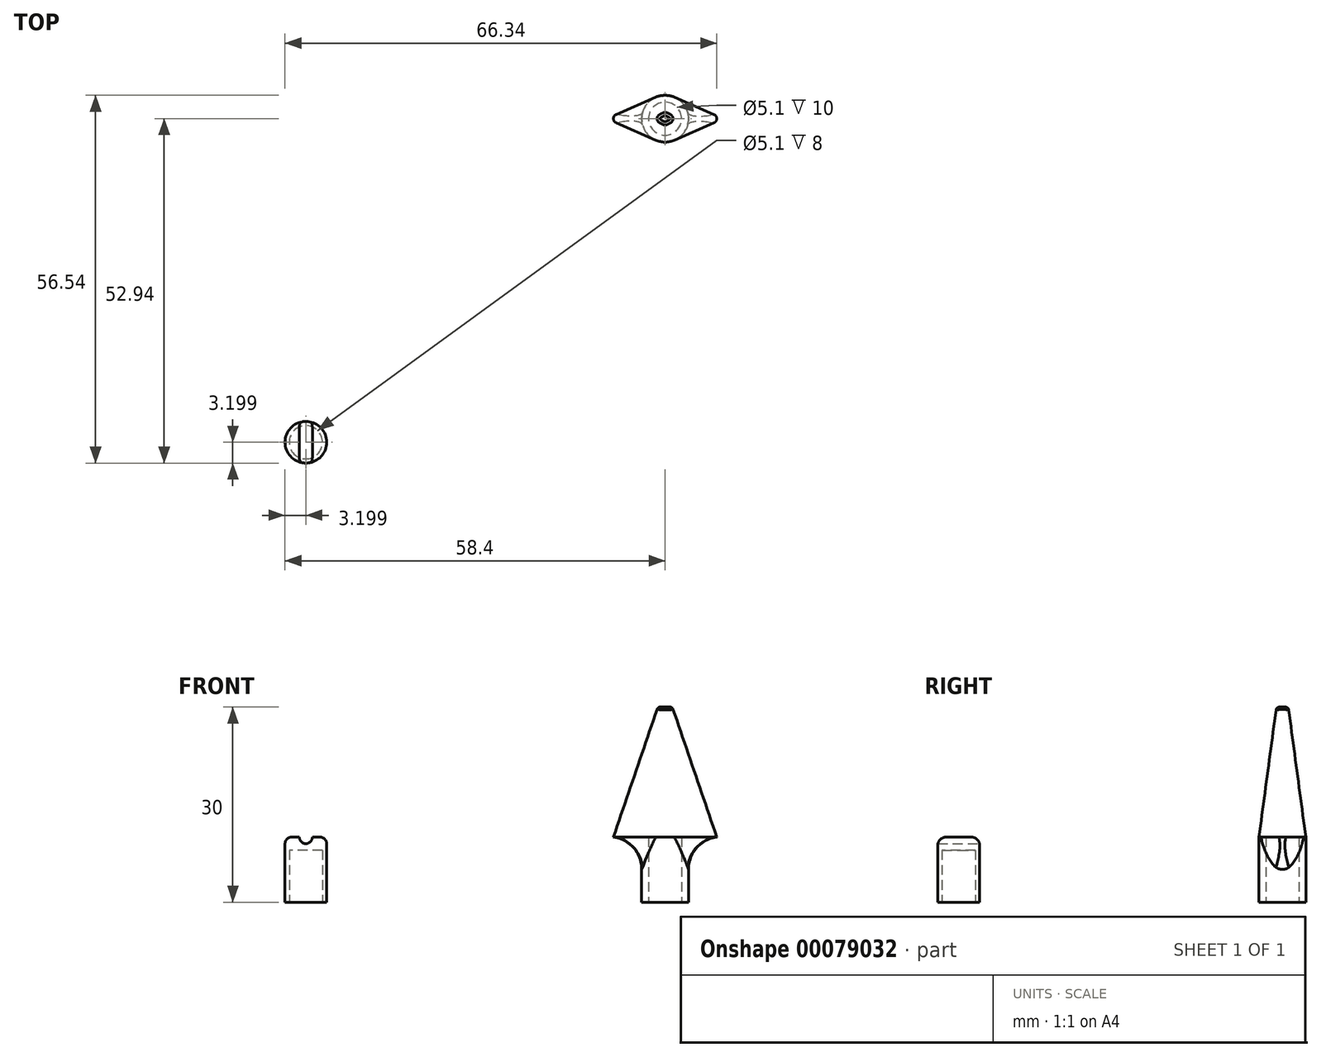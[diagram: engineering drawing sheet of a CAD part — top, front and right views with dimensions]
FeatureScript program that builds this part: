
annotation { "Feature Type Name" : "Feature", "Feature Type Description" : "" }
export const myFeature = defineFeature(function(context is Context, id is Id, definition is map)
    precondition{}
    {
        {
            var Q0;
            Q0=qCreatedBy(makeId("Top.planeOp"),FACE);
            var sketch = newSketch(context, id + "F0", { "sketchPlane" : qUnion([Q0])});
            skCircle(sketch, "E0", {"center": v(0, 0) * mm, "radius": 2.55 * mm});
            skCircle(sketch, "E1", {"center": v(0, 0) * mm, "radius": 3.6 * mm});
            skSolve(sketch);
        }
        {
            var Q0;
            Q0=makeQuery(id+"F0.imprint","IMPRINT",FACE,{"disambiguationData":[TD([[makeQuery(id+"F0.imprint","IMPRINT",EDGE,{"derivedFrom":sQuery(id+"F0.wireOp",EDGE,"E0")}),-1.0]])]});
            extrude(context, id + "F1", {"entities" : qUnion([Q0]), "depth" : 10 * mm});
        }
        {
            var Q0;
            Q0=makeQuery(id+"F1.opExtrude","CAP_FACE",FACE,{"disambiguationData":[OSD([sQuery(id+"F0.wireOp",EDGE,"E0"),sQuery(id+"F0.wireOp",EDGE,"E1")])],"isStart":false});
            var sketch = newSketch(context, id + "F2", { "sketchPlane" : qUnion([Q0])});
            skLineSegment(sketch, "E2", {"start": v(0, 0) * mm, "end": v(0, 3.6) * mm, "construction": true});
            skLineSegment(sketch, "E3", {"start": v(0, 0) * mm, "end": v(0, -3.6) * mm, "construction": true});
            skLineSegment(sketch, "E4", {"start": v(7.51, 0.65) * mm, "end": v(1.44, 3.3) * mm});
            skLineSegment(sketch, "E5.MirrorCS", {"start": v(-7.51, 0.65) * mm, "end": v(-1.44, 3.3) * mm});
            skLineSegment(sketch, "E6.MirrorCS", {"start": v(7.51, -0.65) * mm, "end": v(1.44, -3.3) * mm});
            skLineSegment(sketch, "E7.MirrorCS", {"start": v(-7.51, -0.65) * mm, "end": v(-1.44, -3.3) * mm});
            skPoint(sketch, "E8.visualSharp", {"position": v(9, 0) * mm});
            skArc(sketch, "E8.filletArc", {"start": v(7.51, -0.65) * mm, "mid": v(7.94, 0) * mm, "end": v(7.51, 0.65) * mm});
            skPoint(sketch, "E9.visualSharp", {"position": v(-9, 0) * mm});
            skArc(sketch, "E9.filletArc", {"start": v(-7.51, 0.65) * mm, "mid": v(-7.94, 0) * mm, "end": v(-7.51, -0.65) * mm});
            skArc(sketch, "E10", {"start": v(-1.44, 3.3) * mm, "mid": v(0, 3.6) * mm, "end": v(1.44, 3.3) * mm});
            skArc(sketch, "E11", {"start": v(-1.44, -3.3) * mm, "mid": v(0, -3.6) * mm, "end": v(1.44, -3.3) * mm});
            skSolve(sketch);
        }
        {
            var Q0;
            {var subQ0=sQuery(id+"F2.wireOp",EDGE,"E4");Q0=makeQuery(id+"F2.imprint","IMPRINT",FACE,{"disambiguationData":[TD([[makeQuery(id+"F2.imprint","IMPRINT",EDGE,{"derivedFrom":subQ0}),1.0]])]});}
            cPlane(context, id + "F3", {"entities" : qUnion([Q0]), "cplaneType" : CPlaneType.OFFSET, "offset" : 20 * mm, "width" : 150 * mm, "height" : 150 * mm});
        }
        {
            var Q0;
            Q0=qCreatedBy(id+"F3.planeOp",FACE);
            var sketch = newSketch(context, id + "F4", { "sketchPlane" : qUnion([Q0])});
            skLineSegment(sketch, "E12", {"start": v(0, 0) * mm, "end": v(0, 1) * mm, "construction": true});
            skLineSegment(sketch, "E13", {"start": v(0, 0) * mm, "end": v(0, -1) * mm, "construction": true});
            skLineSegment(sketch, "E14", {"start": v(0.32, 0.83) * mm, "end": v(0.72, 0.63) * mm});
            skLineSegment(sketch, "E15.MirrorCS", {"start": v(-0.32, 0.83) * mm, "end": v(-0.72, 0.63) * mm});
            skLineSegment(sketch, "E16.MirrorCS", {"start": v(0.32, -0.83) * mm, "end": v(0.72, -0.63) * mm});
            skLineSegment(sketch, "E17.MirrorCS", {"start": v(-0.32, -0.83) * mm, "end": v(-0.72, -0.63) * mm});
            skPoint(sketch, "E18.visualSharp", {"position": v(0, 1) * mm});
            skArc(sketch, "E18.filletArc", {"start": v(0.32, 0.83) * mm, "mid": v(0, 0.91) * mm, "end": v(-0.32, 0.83) * mm});
            skPoint(sketch, "E19.visualSharp", {"position": v(1.95, 0) * mm});
            skArc(sketch, "E19.filletArc", {"start": v(0.72, -0.63) * mm, "mid": v(1.1, 0) * mm, "end": v(0.72, 0.63) * mm});
            skPoint(sketch, "E20.visualSharp", {"position": v(0, -1) * mm});
            skArc(sketch, "E20.filletArc", {"start": v(-0.32, -0.83) * mm, "mid": v(0, -0.91) * mm, "end": v(0.32, -0.83) * mm});
            skPoint(sketch, "E21.visualSharp", {"position": v(-1.95, 0) * mm});
            skArc(sketch, "E21.filletArc", {"start": v(-0.72, 0.63) * mm, "mid": v(-1.1, 0) * mm, "end": v(-0.72, -0.63) * mm});
            skSolve(sketch);
        }
        {
            var Q1;
            Q1 = qSketchRegion(id + "F2", true);
            var Q2;
            Q2 = qSketchRegion(id + "F4", true);
            loft(context, id + "F5", {"operationType" : NewBodyOperationType.ADD, "sheetProfilesArray" : [{ "sheetProfileEntities" : qUnion([Q1]) }, { "sheetProfileEntities" : qUnion([Q2]) }]});
        }
        {
            var Q0;
            Q0=makeQuery(id+"F5.boolean.opBoolean","SPLIT",EDGE,{"disambiguationData":[OD(0.0)],"derivedFrom":makeQuery(id+"F1.opExtrude","CAP_EDGE",EDGE,{"disambiguationData":[OSD([sQuery(id+"F0.wireOp",EDGE,"E1")])],"isStart":false})});
            var Q1;
            Q1=makeQuery(id+"F5.boolean.opBoolean","SPLIT",EDGE,{"disambiguationData":[OD(1.0)],"derivedFrom":makeQuery(id+"F1.opExtrude","CAP_EDGE",EDGE,{"disambiguationData":[OSD([sQuery(id+"F0.wireOp",EDGE,"E1")])],"isStart":false})});
            fillet(context, id + "F6", {"entities" : qUnion([Q0, Q1]), "radius" : 5 * mm, "tangentPropagation" : true, "allowEdgeOverflow" : false});
        }
        {
            var Q0;
            Q0=makeQuery(id+"F5.opLoft","MID_CAP_EDGE",EDGE,{"disambiguationData":[OSD([sQuery(id+"F4.wireOp",EDGE,"E15.MirrorCS"),sQuery(id+"F4.wireOp",EDGE,"E17.MirrorCS"),sQuery(id+"F4.wireOp",EDGE,"E21.filletArc")])],"capPos":1.0});
            fillet(context, id + "F7", {"entities" : qUnion([Q0]), "radius" : 0.5 * mm, "tangentPropagation" : true, "allowEdgeOverflow" : false});
        }
        {
            var Q0;
            Q0=qCreatedBy(makeId("Top.planeOp"),FACE);
            var sketch = newSketch(context, id + "F8", { "sketchPlane" : qUnion([Q0])});
            skCircle(sketch, "E22", {"center": v(-55.2, -49.74) * mm, "radius": 2.55 * mm});
            skCircle(sketch, "E23", {"center": v(-55.2, -49.74) * mm, "radius": 3.2 * mm});
            skSolve(sketch);
        }
        {
            var Q0;
            Q0 = qSketchRegion(id + "F8", true);
            extrude(context, id + "F9", {"entities" : qUnion([Q0]), "depth" : 8 * mm});
        }
        {
            var Q0;
            Q0=makeQuery(id+"F9.opExtrude","CAP_FACE",FACE,{"disambiguationData":[OSD([sQuery(id+"F8.wireOp",EDGE,"E22"),sQuery(id+"F8.wireOp",EDGE,"E23")])],"isStart":false});
            var sketch = newSketch(context, id + "F10", { "sketchPlane" : qUnion([Q0])});
            skCircle(sketch, "E24", {"center": v(-55.2, -49.74) * mm, "radius": 3.2 * mm});
            skSolve(sketch);
        }
        {
            var Q0;
            Q0=makeQuery(id+"F10.imprint","IMPRINT",FACE,{"disambiguationData":[TD([[makeQuery(id+"F10.imprint","IMPRINT",EDGE,{"derivedFrom":sQuery(id+"F10.wireOp",EDGE,"E24")}),1.0]])]});
            var Q1;
            Q1=makeQuery(id+"F10.imprint","IMPRINT",FACE,{"disambiguationData":[TD([[makeQuery(id+"F10.imprint","IMPRINT",EDGE,{"derivedFrom":makeQuery(id+"F9.opExtrude","CAP_EDGE",EDGE,{"disambiguationData":[OSD([sQuery(id+"F8.wireOp",EDGE,"E22")])],"isStart":false})}),1.0]])]});
            extrude(context, id + "F11", {"entities" : qUnion([Q0, Q1]), "operationType" : NewBodyOperationType.ADD, "depth" : 2 * mm});
        }
        {
            var Q0;
            Q0=makeQuery(id+"F11.opExtrude","CAP_FACE",FACE,{"disambiguationData":[OSD([sQuery(id+"F10.wireOp",EDGE,"E24")])],"isStart":false});
            var sketch = newSketch(context, id + "F12", { "sketchPlane" : qUnion([Q0])});
            skLineSegment(sketch, "E25", {"start": v(-55.2, -49.74) * mm, "end": v(-55.2, -46.54) * mm, "construction": true});
            skSolve(sketch);
        }
        {
            var Q0;
            Q0=qCreatedBy(makeId("Front.planeOp"),FACE);
            var sketch = newSketch(context, id + "F13", { "sketchPlane" : qUnion([Q0])});
            skCircle(sketch, "E26", {"center": v(-55.2, 10) * mm, "radius": 1 * mm});
            skSolve(sketch);
        }
        {
            var Q0;
            Q0=makeQuery(id+"F13.imprint","IMPRINT",FACE,{"disambiguationData":[TD([[makeQuery(id+"F13.imprint","IMPRINT",EDGE,{"derivedFrom":sQuery(id+"F13.wireOp",EDGE,"E26")}),1.0]])]});
            extrude(context, id + "F14", {"entities" : qUnion([Q0]), "operationType" : NewBodyOperationType.REMOVE, "endBound" : BoundingType.THROUGH_ALL, "depth" : 25 * mm});
        }
        {
            var Q0;
            Q0=makeQuery(id+"F14.boolean.opBoolean","SPLIT",EDGE,{"disambiguationData":[OD(1.0)],"derivedFrom":makeQuery(id+"F11.opExtrude","CAP_EDGE",EDGE,{"disambiguationData":[OSD([sQuery(id+"F10.wireOp",EDGE,"E24")])],"isStart":false})});
            var Q1;
            Q1=makeQuery(id+"F14.boolean.opBoolean","SPLIT",EDGE,{"disambiguationData":[OD(0.0)],"derivedFrom":makeQuery(id+"F11.opExtrude","CAP_EDGE",EDGE,{"disambiguationData":[OSD([sQuery(id+"F10.wireOp",EDGE,"E24")])],"isStart":false})});
            fillet(context, id + "F15", {"entities" : qUnion([Q0, Q1]), "radius" : 1 * mm, "tangentPropagation" : true, "allowEdgeOverflow" : false});
        }
    });
